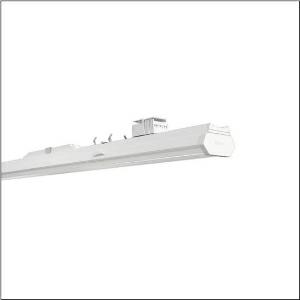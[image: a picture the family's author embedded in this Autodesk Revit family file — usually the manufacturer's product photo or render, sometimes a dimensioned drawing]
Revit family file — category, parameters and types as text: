
# Revit family: licross_r__11_protected_ho_51tp12dn4fxm_edee
name_source: partatom
category: Lighting Fixtures
units: mm (PartAtom-declared; Revit-internal decimal feet)

## family parameters
Cut with Voids When Loaded = No
Host = Face
Light Source = No
Part Type = Normal
Room Calculation Point = No
Round Connector Dimension = Use Diameter
Shared = No

## types (1)
- --- (1 x LED, 15270 lm, 87.3 W, 4000K)
    Apparent Load = 87 VA
    CIE Flux Codes = 70 91 97 98 100
    Color Rendering = 80
    Color Temperature = 4000K
    Default Elevation = 1800 mm
    Description = Licross® 11 Protected HO, luminaire insert, of sheet steel, galvanised, coil coated, white, length: 1.500mm, width: 90mm, height: 101mm, LED rated luminous flux: 15.270lm, light colour: 840, control gear: DALI 2, control gear: ECG DALI, with plug, 5-pole, with phase selection, mains connection: 220..240V, AC, 50/60Hz, halogen-free wiring, primary optical cover: cover, of PMMA, light emission: direct with ceiling illumination distribution, primary light characteristic: symmetric, protection rating (complete): IP64, insulation class (complete): insulation class I (protective earthing), certification: CE, ENEC, VDE, UKCA, protection symbol: D if used in an environment with conductive dust loads with corresponding accessories, impact resistance: IK06, permissible ambient temperature for indoor applications: -25..+30°C, corresponds to IFS (International Featured Standards) requirements for safety and quality in the food industry, reducing of maximum allowable ambient temperature of 5°C with ceiling mounting, LABS conformity tested according to VDMA 24364:2018-05, packaging unit: 1 piece
    Height = 92 mm
    Lamp = 1 x LED
    Lamp Light Flux = 15270 lm
    Lamp Power = 87.3 W
    Lamp count = 1
    Length = 1500 mm
    Luminous efficacy = 175 lm/W
    Manufacturer = Siteco
    ModVariant = No
    Model = 51TP12DN4FXM
    Mounting Place = Ceiling
    Mounting Type = Pendant
    Number of Poles = 1
    OnlyDefault = Yes
    Power Factor = 1
    Product Name = Licross® 11 Protected HO
    Product group = luminaire insert
    ProductGroupID = 902
    Protection Class = Protection class I
    Protection Degree = IP 64
    RLX_Detail_Level = 1
    RlxData = <blob elided: 24429 chars, md5=1864b52b>
    Socket = socket
    Standby Power = 0 W
    System Light Flux = 15270 lm
    System Power = 87 W
    Type Comments = factory setting: luminous flux: 100 % | dim-lin: 254 | 491 mA
    Type Image = l_1256148.jpg
    URL = http://relux.com
    VarID = @adj_002147
    Voltage = 0 V
    Weight = 0.00 kg
    Width = 88 mm

## geometry (parser evidence)
native form markers: Blend x4, Sweep x12
no freeform markers — native parametric forms only
